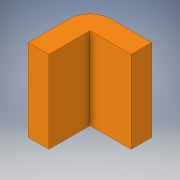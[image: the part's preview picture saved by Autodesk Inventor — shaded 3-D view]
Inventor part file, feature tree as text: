
AUTODESK INVENTOR PART (.ipt)
format: ipt  version: 2017 SP1 (Build 210196100, 196)  size: 97,280 bytes
history: native  units: in
note: dims shown in document units (in); Inventor stores cm internally (conversion verified against a paired STEP export)
features: extrude x1, fillet x1, sketch x1
ambient origin geometry x8: Origin, YZ Plane, XZ Plane, XY Plane, X Axis, Y Axis, Z Axis, Center Point
bodies: Solid1 (feature_tree)
feature tree (3):
  extrude  "Extrusion1"  Depth=0.5in
  fillet  "Fillet1"  Radius=1.5in
  sketch  "Sketch1"  dims[d0=1.5in d1=0.5in d2=1.5in d3=0.5in d4=2.0in d5=0.0in d6=0.5in]
